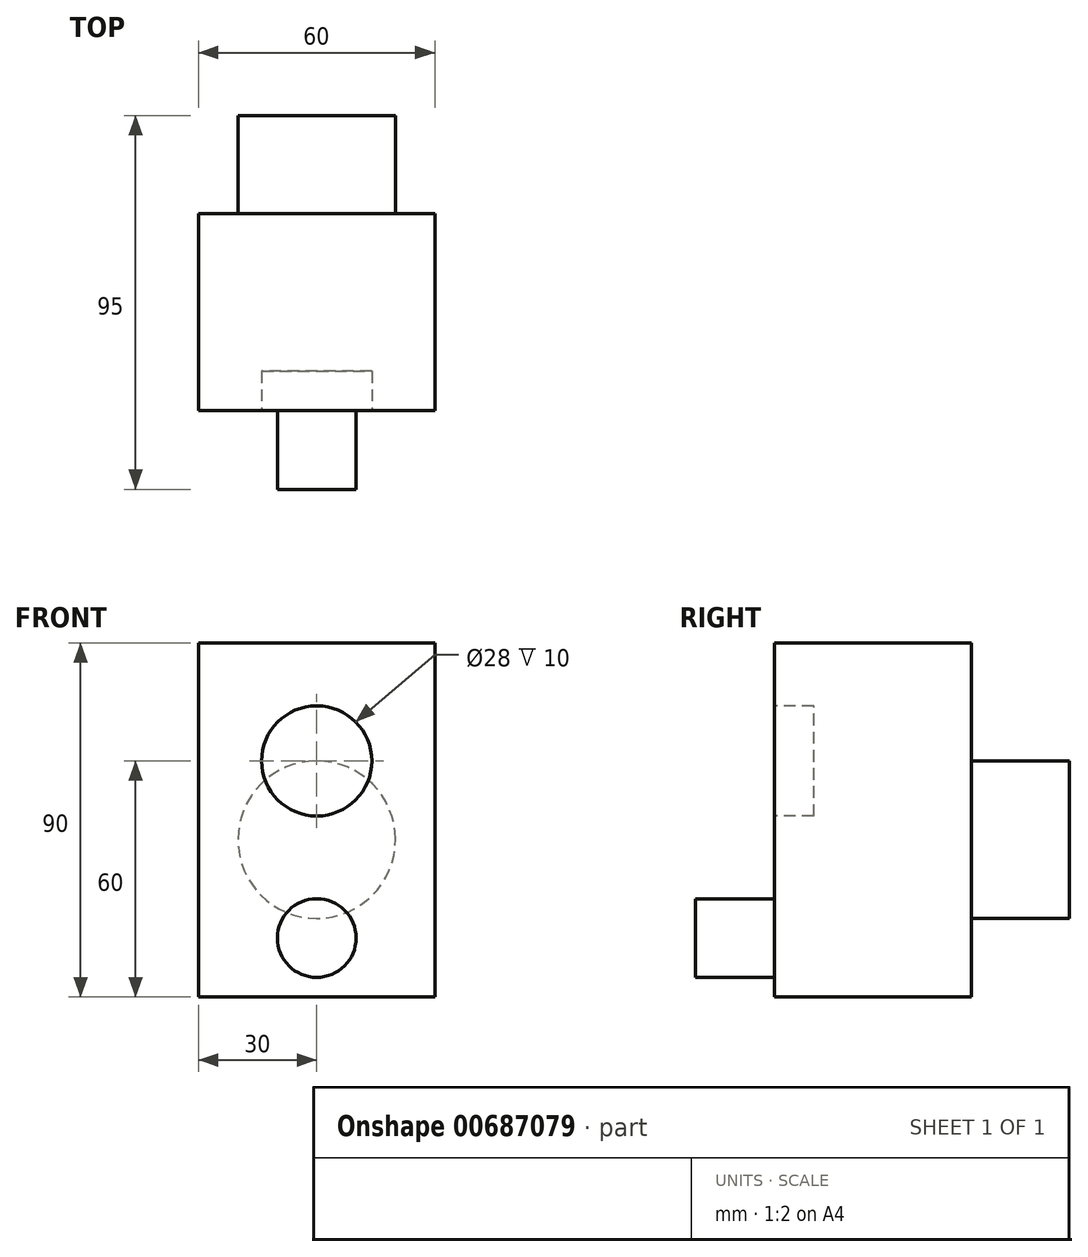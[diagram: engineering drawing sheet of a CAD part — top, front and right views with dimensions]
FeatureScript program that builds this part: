
annotation { "Feature Type Name" : "Feature", "Feature Type Description" : "" }
export const myFeature = defineFeature(function(context is Context, id is Id, definition is map)
    precondition{}
    {
        {
            var Q0;
            Q0=qCreatedBy(makeId("Top.planeOp"),FACE);
            var sketch = newSketch(context, id + "F0", { "sketchPlane" : qUnion([Q0])});
            skLineSegment(sketch, "E0.bottom", {"start": v(30, 30) * mm, "end": v(-30, 30) * mm});
            skLineSegment(sketch, "E0.top", {"start": v(30, -30) * mm, "end": v(-30, -30) * mm});
            skLineSegment(sketch, "E0.left", {"start": v(30, 30) * mm, "end": v(30, -30) * mm});
            skLineSegment(sketch, "E0.right", {"start": v(-30, 30) * mm, "end": v(-30, -30) * mm});
            skPoint(sketch, "E0.middle", {"position": v(0, 0) * mm});
            skSolve(sketch);
        }
        {
            var Q0;
            Q0 = qSketchRegion(id + "F0", true);
            extrude(context, id + "F1", {"entities" : qUnion([Q0]), "depth" : 90 * mm, "offsetDistance" : 25 * mm});
        }
        {
            var Q0;
            Q0=makeQuery(id+"F1.opExtrude","SWEPT_FACE",FACE,{"disambiguationData":[OSD([sQuery(id+"F0.wireOp",EDGE,"E0.top")])]});
            extrude(context, id + "F2", {"entities" : qUnion([Q0]), "operationType" : NewBodyOperationType.ADD, "depth" : 10 * mm, "offsetDistance" : 25 * mm});
        }
        {
            var Q0;
            Q0=makeQuery(id+"F1.opExtrude","SWEPT_FACE",FACE,{"disambiguationData":[OSD([sQuery(id+"F0.wireOp",EDGE,"E0.bottom")])]});
            var sketch = newSketch(context, id + "F3", { "sketchPlane" : qUnion([Q0])});
            skCircle(sketch, "E1", {"center": v(0, 40) * mm, "radius": 20 * mm});
            skLineSegment(sketch, "E2", {"start": v(0, 40) * mm, "end": v(0, 0) * mm});
            skSolve(sketch);
        }
        {
            var Q0;
            Q0 = qSketchRegion(id + "F3", true);
            extrude(context, id + "F4", {"entities" : qUnion([Q0]), "operationType" : NewBodyOperationType.ADD, "depth" : 25 * mm, "offsetDistance" : 25 * mm});
        }
        {
            var Q0;
            Q0=makeQuery(id+"F2.opExtrude","CAP_FACE",FACE,{"disambiguationData":[OSD([sQuery(id+"F0.wireOp",EDGE,"E0.top")])],"isStart":false});
            var sketch = newSketch(context, id + "F5", { "sketchPlane" : qUnion([Q0])});
            skCircle(sketch, "E3", {"center": v(0, 15) * mm, "radius": 10 * mm});
            skSolve(sketch);
        }
        {
            var Q0;
            Q0=makeQuery(id+"F5.imprint","IMPRINT",FACE,{"disambiguationData":[TD([[makeQuery(id+"F5.imprint","IMPRINT",EDGE,{"derivedFrom":sQuery(id+"F5.wireOp",EDGE,"E3")}),-1.0]])]});
            extrude(context, id + "F6", {"entities" : qUnion([Q0]), "operationType" : NewBodyOperationType.REMOVE, "oppositeDirection" : true, "depth" : 20 * mm, "offsetDistance" : 25 * mm});
        }
        {
            var Q0;
            Q0=makeQuery(id+"F6.boolean.opBoolean","COPY",FACE,{"derivedFrom":makeQuery(id+"F6.opExtrude","CAP_FACE",FACE,{"disambiguationData":[OSD([sQuery(id+"F0.wireOp",EDGE,"E0.top"),sQuery(id+"F0.wireOp",EDGE,"E0.left"),sQuery(id+"F0.wireOp",EDGE,"E0.right"),sQuery(id+"F5.wireOp",EDGE,"E3")])],"isStart":false})});
            var sketch = newSketch(context, id + "F7", { "sketchPlane" : qUnion([Q0])});
            skCircle(sketch, "E4", {"center": v(0, 60) * mm, "radius": 14 * mm});
            skSolve(sketch);
        }
        {
            var Q0;
            Q0 = qSketchRegion(id + "F7", true);
            extrude(context, id + "F8", {"entities" : qUnion([Q0]), "operationType" : NewBodyOperationType.REMOVE, "oppositeDirection" : true, "depth" : 10 * mm, "offsetDistance" : 25 * mm});
        }
    });
